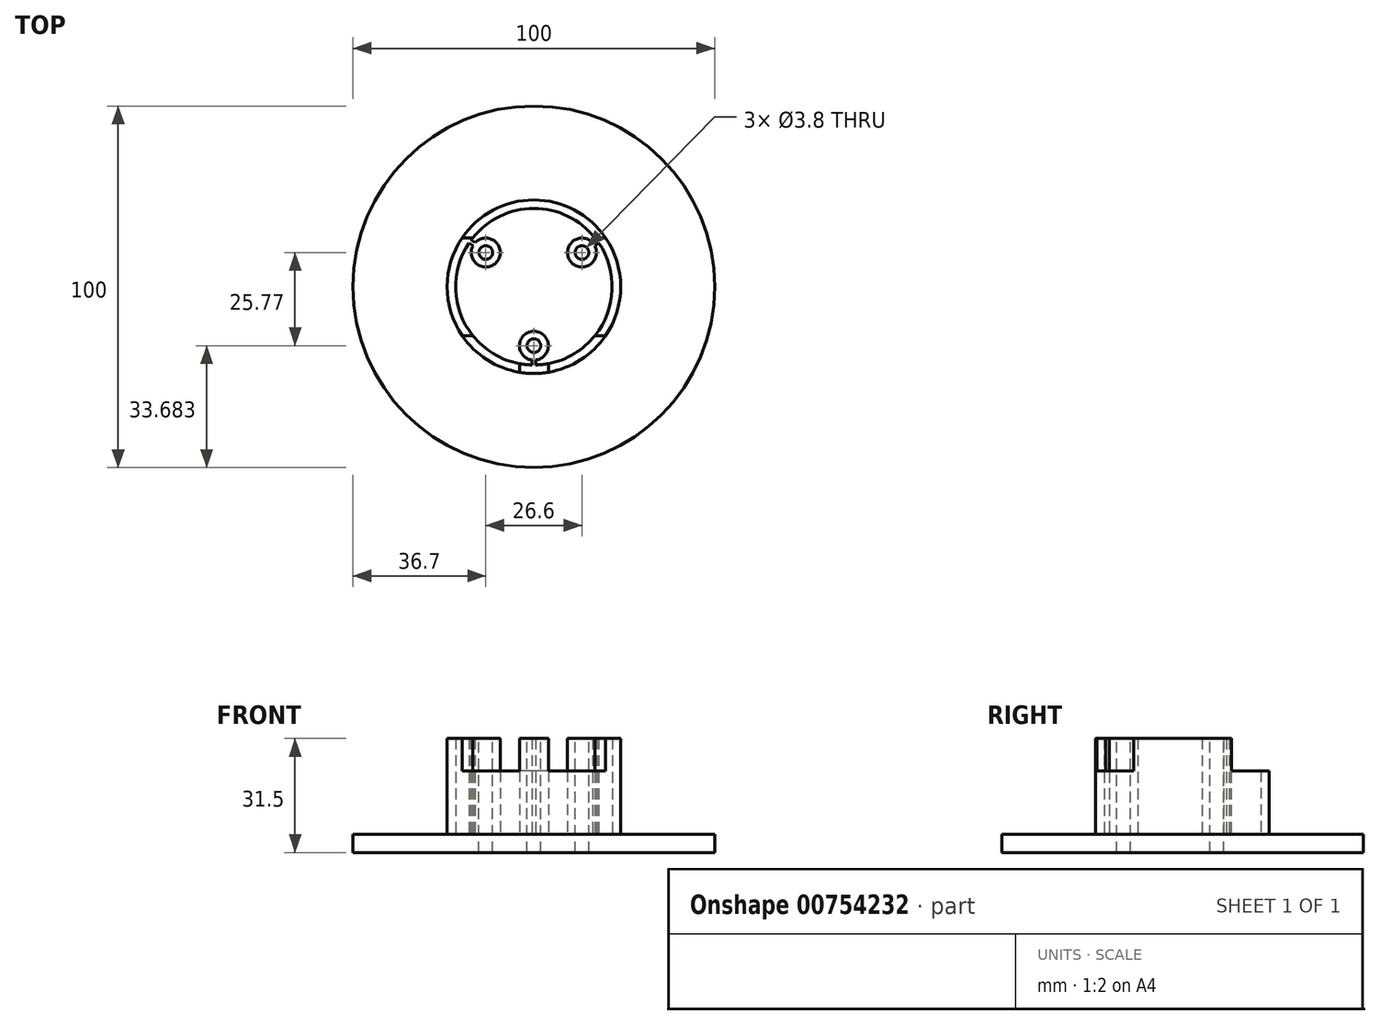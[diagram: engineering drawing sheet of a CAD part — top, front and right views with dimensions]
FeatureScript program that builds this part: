
annotation { "Feature Type Name" : "Feature", "Feature Type Description" : "" }
export const myFeature = defineFeature(function(context is Context, id is Id, definition is map)
    precondition{}
    {
        {
            var Q0;
            Q0=qCreatedBy(makeId("Top.planeOp"),FACE);
            var sketch = newSketch(context, id + "F0", { "sketchPlane" : qUnion([Q0])});
            skCircle(sketch, "E0", {"center": v(0, 0) * mm, "radius": 24 * mm});
            skCircle(sketch, "E1", {"center": v(0, 0) * mm, "radius": 21.65 * mm});
            skLineSegment(sketch, "E2", {"start": v(-19.84, 13.5) * mm, "end": v(19.84, 13.5) * mm, "construction": true});
            skLineSegment(sketch, "E3", {"start": v(-19.84, -13.5) * mm, "end": v(19.84, -13.5) * mm, "construction": true});
            skLineSegment(sketch, "E4", {"start": v(-24, 0) * mm, "end": v(24, 0) * mm, "construction": true});
            skLineSegment(sketch, "E5", {"start": v(0, 24) * mm, "end": v(0, -24) * mm, "construction": true});
            skLineSegment(sketch, "E6", {"start": v(-4, -23.66) * mm, "end": v(-4, -21.28) * mm});
            skLineSegment(sketch, "E7.MirrorCS", {"start": v(4, -23.66) * mm, "end": v(4, -21.28) * mm});
            skCircle(sketch, "E8", {"center": v(0, -16.32) * mm, "radius": 4 * mm});
            skCircle(sketch, "E9", {"center": v(0, -16.32) * mm, "radius": 1.9 * mm});
            skCircle(sketch, "E10.1.0", {"center": v(13.3, 9.45) * mm, "radius": 1.9 * mm});
            skCircle(sketch, "E10.1.1", {"center": v(13.3, 9.45) * mm, "radius": 4 * mm});
            skCircle(sketch, "E10.2.0", {"center": v(-13.3, 9.45) * mm, "radius": 1.9 * mm});
            skCircle(sketch, "E10.2.1", {"center": v(-13.3, 9.45) * mm, "radius": 4 * mm});
            skCircle(sketch, "E11", {"center": v(0, 0) * mm, "radius": 50 * mm});
            skLineSegment(sketch, "E12", {"start": v(-19.84, -13.5) * mm, "end": v(-16.93, -13.5) * mm});
            skLineSegment(sketch, "E13", {"start": v(19.84, -13.5) * mm, "end": v(16.93, -13.5) * mm});
            skLineSegment(sketch, "E14", {"start": v(-19.84, 13.5) * mm, "end": v(-16.93, 13.5) * mm});
            skLineSegment(sketch, "E15", {"start": v(19.84, 13.5) * mm, "end": v(16.93, 13.5) * mm});
            skLineSegment(sketch, "E16", {"start": v(0.5, -21.64) * mm, "end": v(0.5, -20.29) * mm});
            skLineSegment(sketch, "E17.MirrorCS", {"start": v(-0.5, -21.64) * mm, "end": v(-0.5, -20.29) * mm});
            skCircle(sketch, "E18", {"center": v(0, 0) * mm, "radius": 16.32 * mm, "construction": true});
            skLineSegment(sketch, "E19", {"start": v(-13.3, 9.45) * mm, "end": v(13.3, 9.45) * mm, "construction": true});
            skLineSegment(sketch, "E20", {"start": v(0, -16.32) * mm, "end": v(13.3, 9.45) * mm, "construction": true});
            skPoint(sketch, "E21", {"position": v(-11.4, 9.45) * mm});
            skPoint(sketch, "E22", {"position": v(11.4, 9.45) * mm});
            skPoint(sketch, "E23", {"position": v(12.43, 7.76) * mm});
            skPoint(sketch, "E24", {"position": v(0.87, -14.63) * mm});
            skLineSegment(sketch, "E25", {"start": v(0, 0) * mm, "end": v(-17.65, 12.54) * mm, "construction": true});
            skLineSegment(sketch, "E26", {"start": v(-16.25, 12.16) * mm, "end": v(-17.35, 12.95) * mm});
            skLineSegment(sketch, "E27", {"start": v(-16.82, 11.34) * mm, "end": v(-17.93, 12.13) * mm});
            skLineSegment(sketch, "E28.MirrorCS", {"start": v(16.25, 12.16) * mm, "end": v(17.35, 12.95) * mm});
            skLineSegment(sketch, "E29.MirrorCS", {"start": v(16.82, 11.34) * mm, "end": v(17.93, 12.13) * mm});
            skSolve(sketch);
        }
        {
            var Q0;
            Q0 = qSketchRegion(id + "F0", true);
            var Q1;
            {var subQ0=sQuery(id+"F0.wireOp",EDGE,"E7.MirrorCS");Q1=makeQuery(id+"F0.imprint","IMPRINT",FACE,{"disambiguationData":[TD([[makeQuery(id+"F0.imprint","IMPRINT",EDGE,{"derivedFrom":subQ0}),-1.0]])]});}
            var Q2;
            {var subQ0=sQuery(id+"F0.wireOp",EDGE,"E13");Q2=makeQuery(id+"F0.imprint","IMPRINT",FACE,{"disambiguationData":[TD([[makeQuery(id+"F0.imprint","IMPRINT",EDGE,{"derivedFrom":subQ0}),-1.0]])]});}
            var Q3;
            {var subQ0=sQuery(id+"F0.wireOp",EDGE,"E16");Q3=makeQuery(id+"F0.imprint","IMPRINT",FACE,{"disambiguationData":[TD([[makeQuery(id+"F0.imprint","IMPRINT",EDGE,{"derivedFrom":subQ0}),-1.0]])]});}
            var Q4;
            {var subQ0=sQuery(id+"F0.wireOp",EDGE,"E14");Q4=makeQuery(id+"F0.imprint","IMPRINT",FACE,{"disambiguationData":[TD([[makeQuery(id+"F0.imprint","IMPRINT",EDGE,{"derivedFrom":subQ0}),1.0]])]});}
            var Q5;
            Q5=makeQuery(id+"F0.imprint","IMPRINT",FACE,{"disambiguationData":[TD([[makeQuery(id+"F0.imprint","IMPRINT",EDGE,{"derivedFrom":sQuery(id+"F0.wireOp",EDGE,"E10.2.0")}),-1.0]])]});
            var Q6;
            Q6=makeQuery(id+"F0.imprint","IMPRINT",FACE,{"disambiguationData":[TD([[makeQuery(id+"F0.imprint","IMPRINT",EDGE,{"derivedFrom":sQuery(id+"F0.wireOp",EDGE,"E10.1.0")}),-1.0]])]});
            var Q7;
            {var subQ0=sQuery(id+"F0.wireOp",EDGE,"ba92d170-98f2-49b8-8035-852a67a62ef7.1.0");Q7=makeQuery(id+"F0.imprint","IMPRINT",FACE,{"disambiguationData":[TD([[makeQuery(id+"F0.imprint","IMPRINT",EDGE,{"derivedFrom":subQ0}),1.0]])]});}
            var Q8;
            {var subQ0=sQuery(id+"F0.wireOp",EDGE,"ba92d170-98f2-49b8-8035-852a67a62ef7.2.0");Q8=makeQuery(id+"F0.imprint","IMPRINT",FACE,{"disambiguationData":[TD([[makeQuery(id+"F0.imprint","IMPRINT",EDGE,{"derivedFrom":subQ0}),1.0]])]});}
            var Q9;
            {var subQ4=sQuery(id+"F0.wireOp",EDGE,"E12");Q9=makeQuery(id+"F0.imprint","IMPRINT",FACE,{"disambiguationData":[TD([[makeQuery(id+"F0.imprint","IMPRINT",EDGE,{"derivedFrom":subQ4}),1.0]])]});}
            var Q10;
            {var subQ0=sQuery(id+"F0.wireOp",EDGE,"E6");Q10=makeQuery(id+"F0.imprint","IMPRINT",FACE,{"disambiguationData":[TD([[makeQuery(id+"F0.imprint","IMPRINT",EDGE,{"derivedFrom":subQ0}),1.0]])]});}
            var Q11;
            {var subQ4=sQuery(id+"F0.wireOp",EDGE,"E6");Q11=makeQuery(id+"F0.imprint","IMPRINT",FACE,{"disambiguationData":[TD([[makeQuery(id+"F0.imprint","IMPRINT",EDGE,{"derivedFrom":subQ4}),-1.0]])]});}
            var Q12;
            Q12=makeQuery(id+"F0.imprint","IMPRINT",FACE,{"disambiguationData":[TD([[makeQuery(id+"F0.imprint","IMPRINT",EDGE,{"derivedFrom":sQuery(id+"F0.wireOp",EDGE,"E9")}),-1.0]])]});
            var Q13;
            {var subQ0=sQuery(id+"F0.wireOp",EDGE,"E16");Q13=makeQuery(id+"F0.imprint","IMPRINT",FACE,{"disambiguationData":[TD([[makeQuery(id+"F0.imprint","IMPRINT",EDGE,{"derivedFrom":subQ0}),1.0]])]});}
            var Q14;
            {var subQ0=sQuery(id+"F0.wireOp",EDGE,"E28.MirrorCS");Q14=makeQuery(id+"F0.imprint","IMPRINT",FACE,{"disambiguationData":[TD([[makeQuery(id+"F0.imprint","IMPRINT",EDGE,{"derivedFrom":subQ0}),-1.0]])]});}
            var Q15;
            {var subQ0=sQuery(id+"F0.wireOp",EDGE,"E26");Q15=makeQuery(id+"F0.imprint","IMPRINT",FACE,{"disambiguationData":[TD([[makeQuery(id+"F0.imprint","IMPRINT",EDGE,{"derivedFrom":subQ0}),1.0]])]});}
            extrude(context, id + "F1", {"entities" : qUnion([Q0, Q1, Q2, Q3, Q4, Q5, Q6, Q7, Q8, Q9, Q10, Q11, Q12, Q13, Q14, Q15]), "oppositeDirection" : true, "depth" : 5 * mm, "offsetDistance" : 25 * mm});
        }
        {
            var Q0;
            {var subQ0=sQuery(id+"F0.wireOp",EDGE,"E7.MirrorCS");Q0=makeQuery(id+"F0.imprint","IMPRINT",FACE,{"disambiguationData":[TD([[makeQuery(id+"F0.imprint","IMPRINT",EDGE,{"derivedFrom":subQ0}),-1.0]])]});}
            var Q1;
            {var subQ0=sQuery(id+"F0.wireOp",EDGE,"E6");Q1=makeQuery(id+"F0.imprint","IMPRINT",FACE,{"disambiguationData":[TD([[makeQuery(id+"F0.imprint","IMPRINT",EDGE,{"derivedFrom":subQ0}),1.0]])]});}
            var Q2;
            {var subQ0=sQuery(id+"F0.wireOp",EDGE,"E14");Q2=makeQuery(id+"F0.imprint","IMPRINT",FACE,{"disambiguationData":[TD([[makeQuery(id+"F0.imprint","IMPRINT",EDGE,{"derivedFrom":subQ0}),1.0]])]});}
            extrude(context, id + "F2", {"entities" : qUnion([Q0, Q1, Q2]), "operationType" : NewBodyOperationType.ADD, "depth" : 17.5 * mm, "offsetDistance" : 25 * mm});
        }
        {
            var Q0;
            {var subQ4=sQuery(id+"F0.wireOp",EDGE,"E12");Q0=makeQuery(id+"F0.imprint","IMPRINT",FACE,{"disambiguationData":[TD([[makeQuery(id+"F0.imprint","IMPRINT",EDGE,{"derivedFrom":subQ4}),1.0]])]});}
            var Q1;
            {var subQ0=sQuery(id+"F0.wireOp",EDGE,"E13");Q1=makeQuery(id+"F0.imprint","IMPRINT",FACE,{"disambiguationData":[TD([[makeQuery(id+"F0.imprint","IMPRINT",EDGE,{"derivedFrom":subQ0}),-1.0]])]});}
            var Q2;
            {var subQ0=sQuery(id+"F0.wireOp",EDGE,"ba92d170-98f2-49b8-8035-852a67a62ef7.1.0");Q2=makeQuery(id+"F0.imprint","IMPRINT",FACE,{"disambiguationData":[TD([[makeQuery(id+"F0.imprint","IMPRINT",EDGE,{"derivedFrom":subQ0}),1.0]])]});}
            var Q3;
            Q3=makeQuery(id+"F0.imprint","IMPRINT",FACE,{"disambiguationData":[TD([[makeQuery(id+"F0.imprint","IMPRINT",EDGE,{"derivedFrom":sQuery(id+"F0.wireOp",EDGE,"E10.1.0")}),-1.0]])]});
            var Q4;
            Q4=makeQuery(id+"F0.imprint","IMPRINT",FACE,{"disambiguationData":[TD([[makeQuery(id+"F0.imprint","IMPRINT",EDGE,{"derivedFrom":sQuery(id+"F0.wireOp",EDGE,"E9")}),-1.0]])]});
            var Q5;
            {var subQ0=sQuery(id+"F0.wireOp",EDGE,"E16");Q5=makeQuery(id+"F0.imprint","IMPRINT",FACE,{"disambiguationData":[TD([[makeQuery(id+"F0.imprint","IMPRINT",EDGE,{"derivedFrom":subQ0}),1.0]])]});}
            var Q6;
            {var subQ4=sQuery(id+"F0.wireOp",EDGE,"E6");Q6=makeQuery(id+"F0.imprint","IMPRINT",FACE,{"disambiguationData":[TD([[makeQuery(id+"F0.imprint","IMPRINT",EDGE,{"derivedFrom":subQ4}),-1.0]])]});}
            var Q7;
            {var subQ0=sQuery(id+"F0.wireOp",EDGE,"ba92d170-98f2-49b8-8035-852a67a62ef7.2.0");Q7=makeQuery(id+"F0.imprint","IMPRINT",FACE,{"disambiguationData":[TD([[makeQuery(id+"F0.imprint","IMPRINT",EDGE,{"derivedFrom":subQ0}),1.0]])]});}
            var Q8;
            Q8=makeQuery(id+"F0.imprint","IMPRINT",FACE,{"disambiguationData":[TD([[makeQuery(id+"F0.imprint","IMPRINT",EDGE,{"derivedFrom":sQuery(id+"F0.wireOp",EDGE,"E10.2.0")}),-1.0]])]});
            var Q9;
            {var subQ0=sQuery(id+"F0.wireOp",EDGE,"E26");Q9=makeQuery(id+"F0.imprint","IMPRINT",FACE,{"disambiguationData":[TD([[makeQuery(id+"F0.imprint","IMPRINT",EDGE,{"derivedFrom":subQ0}),1.0]])]});}
            var Q10;
            {var subQ0=sQuery(id+"F0.wireOp",EDGE,"E28.MirrorCS");Q10=makeQuery(id+"F0.imprint","IMPRINT",FACE,{"disambiguationData":[TD([[makeQuery(id+"F0.imprint","IMPRINT",EDGE,{"derivedFrom":subQ0}),-1.0]])]});}
            extrude(context, id + "F3", {"entities" : qUnion([Q0, Q1, Q2, Q3, Q4, Q5, Q6, Q7, Q8, Q9, Q10]), "operationType" : NewBodyOperationType.ADD, "depth" : (17.5 + 9) * mm, "offsetDistance" : 25 * mm});
        }
    });
